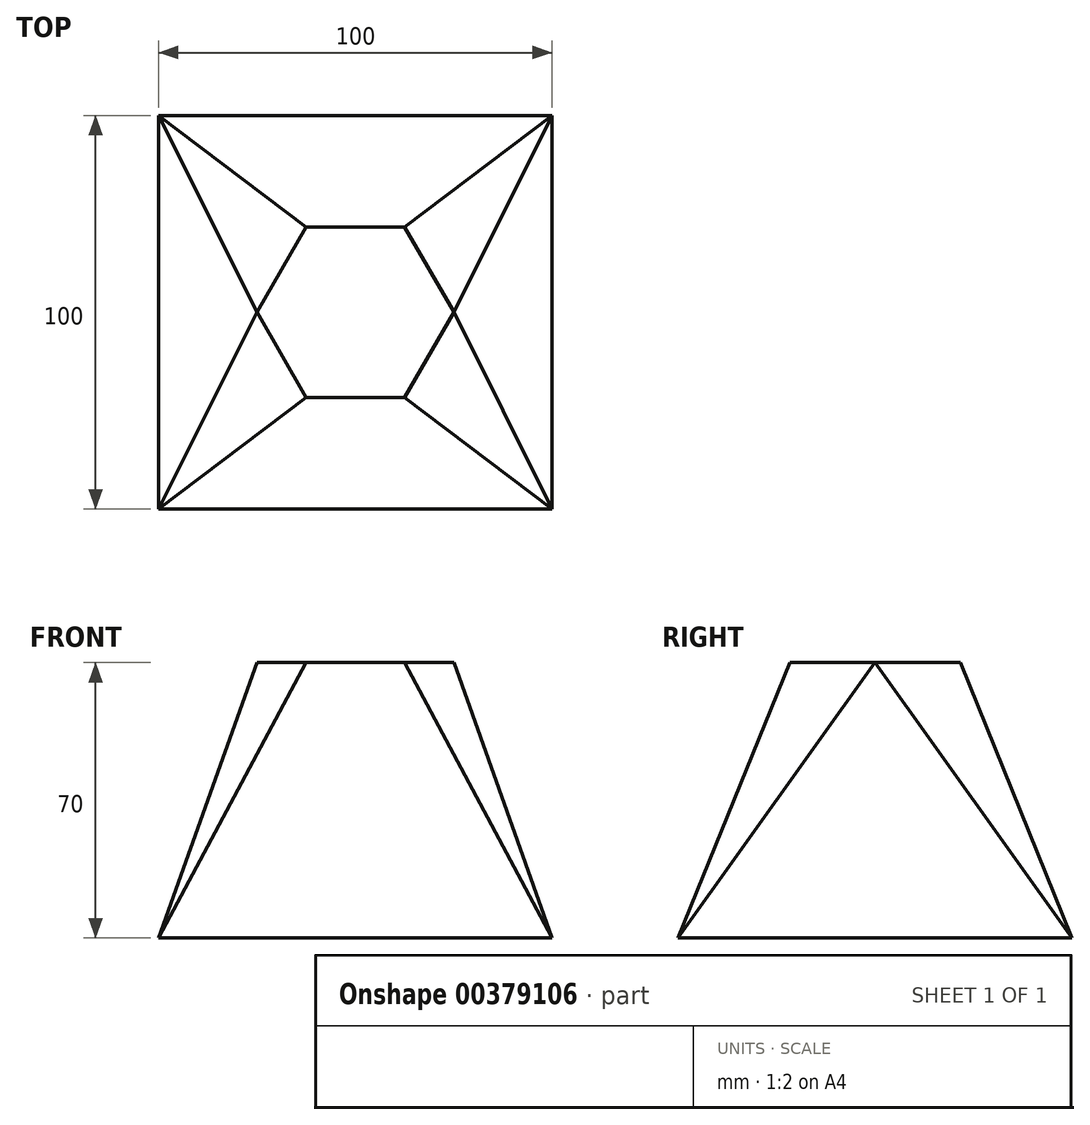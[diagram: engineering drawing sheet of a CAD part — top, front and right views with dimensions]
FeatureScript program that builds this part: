
annotation { "Feature Type Name" : "Feature", "Feature Type Description" : "" }
export const myFeature = defineFeature(function(context is Context, id is Id, definition is map)
    precondition{}
    {
        {
            var Q0;
            Q0=qCreatedBy(makeId("Top.planeOp"),FACE);
            var sketch = newSketch(context, id + "F0", { "sketchPlane" : qUnion([Q0])});
            skLineSegment(sketch, "E0.bottom", {"start": v(50, 50) * mm, "end": v(-50, 50) * mm});
            skLineSegment(sketch, "E0.top", {"start": v(50, -50) * mm, "end": v(-50, -50) * mm});
            skLineSegment(sketch, "E0.left", {"start": v(50, 50) * mm, "end": v(50, -50) * mm});
            skLineSegment(sketch, "E0.right", {"start": v(-50, 50) * mm, "end": v(-50, -50) * mm});
            skPoint(sketch, "E0.middle", {"position": v(0, 0) * mm});
            skSolve(sketch);
        }
        {
            var Q0;
            Q0=qCreatedBy(makeId("Top.planeOp"),FACE);
            cPlane(context, id + "F1", {"entities" : qUnion([Q0]), "cplaneType" : CPlaneType.OFFSET, "offset" : 70 * mm, "width" : 150 * mm, "height" : 150 * mm});
        }
        {
            var Q0;
            Q0=qCreatedBy(id+"F1.planeOp",FACE);
            var sketch = newSketch(context, id + "F2", { "sketchPlane" : qUnion([Q0])});
            skCircle(sketch, "E1.cCircle", {"center": v(0, 0) * mm, "radius": 21.65 * mm, "construction": true});
            skLineSegment(sketch, "E1.0", {"start": v(-12.5, 21.65) * mm, "end": v(12.5, 21.65) * mm});
            skLineSegment(sketch, "E1.1", {"start": v(12.5, 21.65) * mm, "end": v(25, 0) * mm});
            skLineSegment(sketch, "E1.2", {"start": v(25, 0) * mm, "end": v(12.5, -21.65) * mm});
            skLineSegment(sketch, "E1.3", {"start": v(12.5, -21.65) * mm, "end": v(-12.5, -21.65) * mm});
            skLineSegment(sketch, "E1.4", {"start": v(-12.5, -21.65) * mm, "end": v(-25, 0) * mm});
            skLineSegment(sketch, "E1.5", {"start": v(-25, 0) * mm, "end": v(-12.5, 21.65) * mm});
            skPoint(sketch, "E1.0.midPoint", {"position": v(0, 21.65) * mm});
            skLineSegment(sketch, "E2.bottom", {"start": v(25, 21.65) * mm, "end": v(-25, 21.65) * mm});
            skLineSegment(sketch, "E2.top", {"start": v(25, -21.65) * mm, "end": v(-25, -21.65) * mm});
            skLineSegment(sketch, "E2.left", {"start": v(25, 21.65) * mm, "end": v(25, -21.65) * mm});
            skLineSegment(sketch, "E2.right", {"start": v(-25, 21.65) * mm, "end": v(-25, -21.65) * mm});
            skSolve(sketch);
        }
        {
            var Q0;
            Q0=qCreatedBy(id+"F1.planeOp",FACE);
            var sketch = newSketch(context, id + "F3", { "sketchPlane" : qUnion([Q0])});
            skLineSegment(sketch, "E3.bottom", {"start": v(25, 21.65) * mm, "end": v(-25, 21.65) * mm});
            skLineSegment(sketch, "E3.top", {"start": v(25, -21.65) * mm, "end": v(-25, -21.65) * mm});
            skLineSegment(sketch, "E3.left", {"start": v(25, 21.65) * mm, "end": v(25, -21.65) * mm});
            skLineSegment(sketch, "E3.right", {"start": v(-25, 21.65) * mm, "end": v(-25, -21.65) * mm});
            skPoint(sketch, "E3.middle", {"position": v(0, 0) * mm});
            skSolve(sketch);
        }
        {
            var Q0;
            Q0=makeQuery(id+"F0.imprint","IMPRINT",FACE,{"disambiguationData":[TD([[makeQuery(id+"F0.imprint","IMPRINT",EDGE,{"derivedFrom":sQuery(id+"F0.wireOp",EDGE,"E0.bottom")}),1.0]])]});
            var Q1;
            Q1=makeQuery(id+"F3.imprint","IMPRINT",FACE,{"disambiguationData":[TD([[makeQuery(id+"F3.imprint","IMPRINT",EDGE,{"derivedFrom":sQuery(id+"F3.wireOp",EDGE,"E3.bottom")}),1.0]])]});
            loft(context, id + "F4", {"sheetProfilesArray" : [{ "sheetProfileEntities" : qUnion([Q0]) }, { "sheetProfileEntities" : qUnion([Q1]) }]});
        }
        {
            var Q1;
            {var subQ0=sQuery(id+"F2.wireOp",EDGE,"E1.4");Q1=makeQuery(id+"F2.imprint","IMPRINT",FACE,{"disambiguationData":[TD([[makeQuery(id+"F2.imprint","IMPRINT",EDGE,{"derivedFrom":subQ0}),1.0]])]});}
            var Q2;
            Q2=makeQuery(id+"F4.opLoft","MID_CAP_VERTEX",VERTEX,{"disambiguationData":[OSD([sQuery(id+"F0.wireOp",EDGE,"E0.top"),sQuery(id+"F0.wireOp",EDGE,"E0.right")])],"capPos":0.0});
            loft(context, id + "F5", {"sheetProfilesArray" : [{ "sheetProfileEntities" : qUnion([Q1]) }, { "sheetProfileEntities" : qUnion([Q2]) }]});
        }
        {
            var Q0;
            {var subQ0=sQuery(id+"F2.wireOp",EDGE,"E1.4");Q0=makeQuery(id+"F5.opLoft","SWEPT_BODY",BODY,{"disambiguationData":[OSD([sQuery(id+"F0.wireOp",EDGE,"E0.top"),sQuery(id+"F0.wireOp",EDGE,"E0.right"),makeQuery(id+"F2.imprint","IMPRINT",FACE,{"disambiguationData":[TD([[makeQuery(id+"F2.imprint","IMPRINT",EDGE,{"derivedFrom":subQ0}),1.0]])]})])]});}
            var Q1;
            Q1=qCreatedBy(makeId("Right.planeOp"),FACE);
            mirror(context, id + "F6", {"entities" : qUnion([Q0]), "mirrorPlane" : qUnion([Q1])});
        }
        {
            var Q0;
            {var subQ0=sQuery(id+"F2.wireOp",EDGE,"E1.4");Q0=makeQuery(id+"F5.opLoft","SWEPT_BODY",BODY,{"disambiguationData":[OSD([sQuery(id+"F0.wireOp",EDGE,"E0.top"),sQuery(id+"F0.wireOp",EDGE,"E0.right"),makeQuery(id+"F2.imprint","IMPRINT",FACE,{"disambiguationData":[TD([[makeQuery(id+"F2.imprint","IMPRINT",EDGE,{"derivedFrom":subQ0}),1.0]])]})])]});}
            var Q1;
            {var subQ0=sQuery(id+"F2.wireOp",EDGE,"E1.4");Q1=makeQuery(id+"F6.opPattern","COPY",BODY,{"derivedFrom":makeQuery(id+"F5.opLoft","SWEPT_BODY",BODY,{"disambiguationData":[OSD([sQuery(id+"F0.wireOp",EDGE,"E0.top"),sQuery(id+"F0.wireOp",EDGE,"E0.right"),makeQuery(id+"F2.imprint","IMPRINT",FACE,{"disambiguationData":[TD([[makeQuery(id+"F2.imprint","IMPRINT",EDGE,{"derivedFrom":subQ0}),1.0]])]})])]}),"instanceName":"1"});}
            var Q2;
            Q2=qCreatedBy(makeId("Front.planeOp"),FACE);
            mirror(context, id + "F7", {"entities" : qUnion([Q0, Q1]), "mirrorPlane" : qUnion([Q2])});
        }
        {
            var Q0;
            {var subQ0=sQuery(id+"F2.wireOp",EDGE,"E1.4");Q0=makeQuery(id+"F5.opLoft","SWEPT_BODY",BODY,{"disambiguationData":[OSD([sQuery(id+"F0.wireOp",EDGE,"E0.top"),sQuery(id+"F0.wireOp",EDGE,"E0.right"),makeQuery(id+"F2.imprint","IMPRINT",FACE,{"disambiguationData":[TD([[makeQuery(id+"F2.imprint","IMPRINT",EDGE,{"derivedFrom":subQ0}),1.0]])]})])]});}
            var Q1;
            {var subQ0=sQuery(id+"F2.wireOp",EDGE,"E1.4");Q1=makeQuery(id+"F6.opPattern","COPY",BODY,{"derivedFrom":makeQuery(id+"F5.opLoft","SWEPT_BODY",BODY,{"disambiguationData":[OSD([sQuery(id+"F0.wireOp",EDGE,"E0.top"),sQuery(id+"F0.wireOp",EDGE,"E0.right"),makeQuery(id+"F2.imprint","IMPRINT",FACE,{"disambiguationData":[TD([[makeQuery(id+"F2.imprint","IMPRINT",EDGE,{"derivedFrom":subQ0}),1.0]])]})])]}),"instanceName":"1"});}
            var Q2;
            {var subQ0=sQuery(id+"F2.wireOp",EDGE,"E1.4");Q2=makeQuery(id+"F7.opPattern","COPY",BODY,{"derivedFrom":makeQuery(id+"F5.opLoft","SWEPT_BODY",BODY,{"disambiguationData":[OSD([sQuery(id+"F0.wireOp",EDGE,"E0.top"),sQuery(id+"F0.wireOp",EDGE,"E0.right"),makeQuery(id+"F2.imprint","IMPRINT",FACE,{"disambiguationData":[TD([[makeQuery(id+"F2.imprint","IMPRINT",EDGE,{"derivedFrom":subQ0}),1.0]])]})])]}),"instanceName":"1"});}
            var Q3;
            {var subQ0=sQuery(id+"F2.wireOp",EDGE,"E1.4");Q3=makeQuery(id+"F7.opPattern","COPY",BODY,{"derivedFrom":makeQuery(id+"F6.opPattern","COPY",BODY,{"derivedFrom":makeQuery(id+"F5.opLoft","SWEPT_BODY",BODY,{"disambiguationData":[OSD([sQuery(id+"F0.wireOp",EDGE,"E0.top"),sQuery(id+"F0.wireOp",EDGE,"E0.right"),makeQuery(id+"F2.imprint","IMPRINT",FACE,{"disambiguationData":[TD([[makeQuery(id+"F2.imprint","IMPRINT",EDGE,{"derivedFrom":subQ0}),1.0]])]})])]}),"instanceName":"1"}),"instanceName":"1"});}
            var Q4;
            Q4=makeQuery(id+"F4.opLoft","SWEPT_BODY",BODY,{"disambiguationData":[OSD([makeQuery(id+"F0.imprint","IMPRINT",FACE,{"disambiguationData":[TD([[makeQuery(id+"F0.imprint","IMPRINT",EDGE,{"derivedFrom":sQuery(id+"F0.wireOp",EDGE,"E0.bottom")}),1.0]])]}),makeQuery(id+"F3.imprint","IMPRINT",FACE,{"disambiguationData":[TD([[makeQuery(id+"F3.imprint","IMPRINT",EDGE,{"derivedFrom":sQuery(id+"F3.wireOp",EDGE,"E3.bottom")}),1.0]])]})])]});
            booleanBodies(context, id + "F8", {"operationType" : BooleanOperationType.SUBTRACTION, "tools" : qUnion([Q0, Q1, Q2, Q3]), "targets" : qUnion([Q4])});
        }
    });
